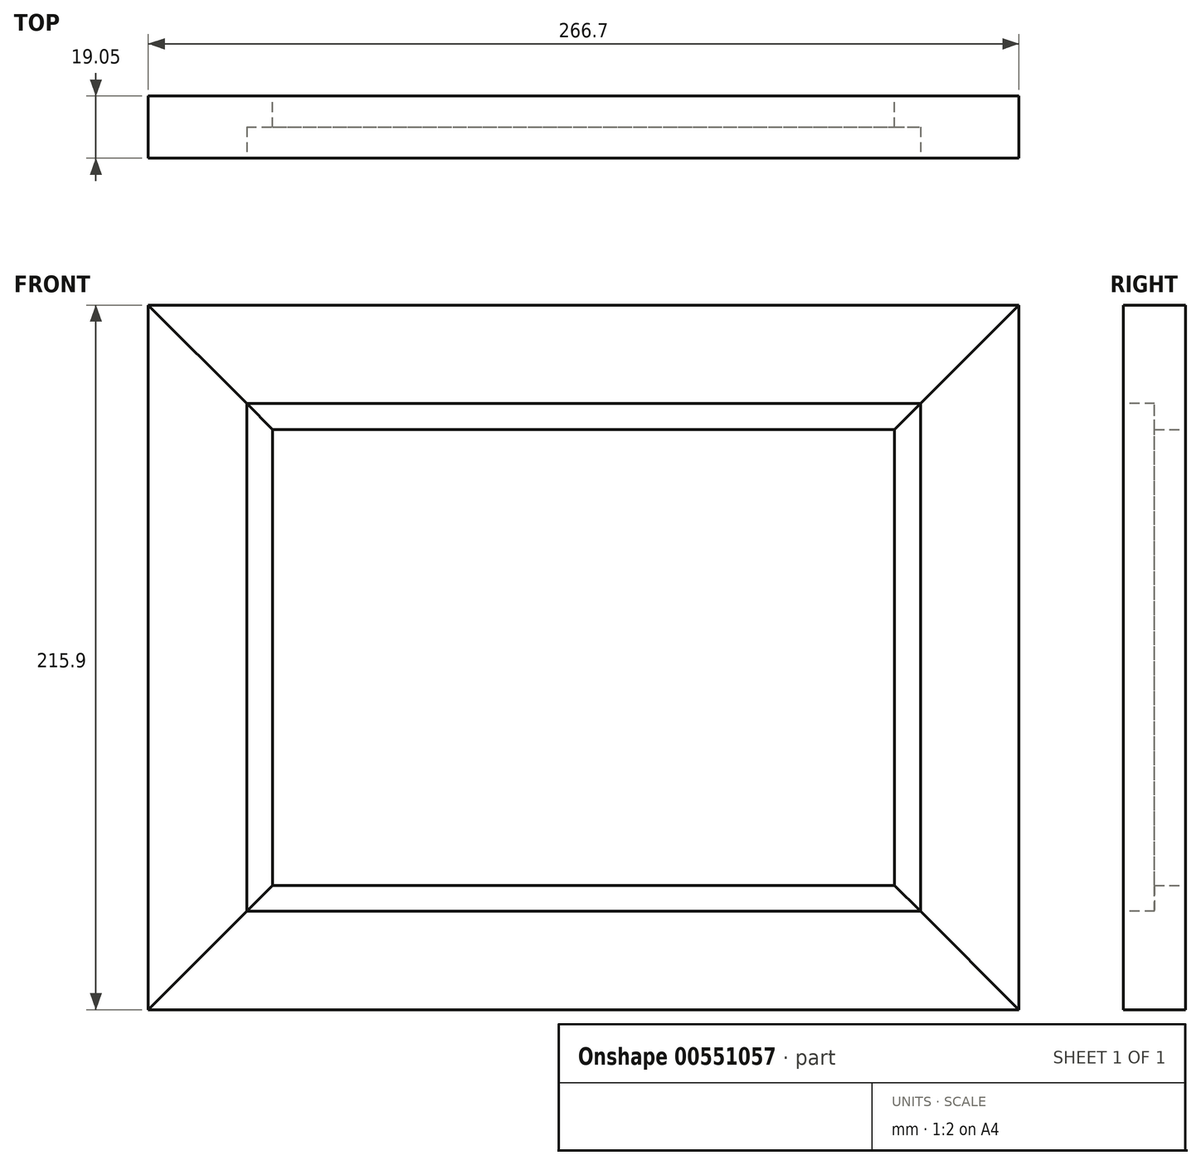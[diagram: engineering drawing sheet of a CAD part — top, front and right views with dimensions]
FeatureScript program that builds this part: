
annotation { "Feature Type Name" : "Feature", "Feature Type Description" : "" }
export const myFeature = defineFeature(function(context is Context, id is Id, definition is map)
    precondition{}
    {
        {
            var Q0;
            Q0=qCreatedBy(makeId("Front.planeOp"),FACE);
            var sketch = newSketch(context, id + "F0", { "sketchPlane" : qUnion([Q0])});
            skLineSegment(sketch, "E0", {"start": v(0, 0) * mm, "end": v(0, 139.7) * mm});
            skLineSegment(sketch, "E1", {"start": v(0, 139.7) * mm, "end": v(-38.1, 177.8) * mm});
            skLineSegment(sketch, "E2", {"start": v(-38.1, 177.8) * mm, "end": v(-38.1, -38.1) * mm});
            skLineSegment(sketch, "E3", {"start": v(-38.1, -38.1) * mm, "end": v(0, 0) * mm});
            skLineSegment(sketch, "E4", {"start": v(0, 139.7) * mm, "end": v(190.5, 139.7) * mm});
            skLineSegment(sketch, "E5", {"start": v(190.5, 139.7) * mm, "end": v(228.6, 177.8) * mm});
            skLineSegment(sketch, "E6", {"start": v(228.6, 177.8) * mm, "end": v(-38.1, 177.8) * mm});
            skLineSegment(sketch, "E7", {"start": v(0, 0) * mm, "end": v(190.5, 0) * mm});
            skLineSegment(sketch, "E8", {"start": v(190.5, 0) * mm, "end": v(190.5, 139.7) * mm});
            skLineSegment(sketch, "E9", {"start": v(190.5, 0) * mm, "end": v(228.6, -38.1) * mm});
            skLineSegment(sketch, "E10", {"start": v(228.6, -38.1) * mm, "end": v(228.6, 177.8) * mm});
            skLineSegment(sketch, "E11", {"start": v(-38.1, -38.1) * mm, "end": v(228.6, -38.1) * mm});
            skSolve(sketch);
        }
        {
            var Q0;
            Q0=makeQuery(id+"F0.imprint","IMPRINT",FACE,{"disambiguationData":[TD([[makeQuery(id+"F0.imprint","IMPRINT",EDGE,{"derivedFrom":sQuery(id+"F0.wireOp",EDGE,"E0")}),1.0]])]});
            extrude(context, id + "F1", {"entities" : qUnion([Q0]), "depth" : 19.05 * mm, "offsetDistance" : 25.4 * mm});
        }
        {
            var Q0;
            Q0=makeQuery(id+"F0.imprint","IMPRINT",FACE,{"disambiguationData":[TD([[makeQuery(id+"F0.imprint","IMPRINT",EDGE,{"derivedFrom":sQuery(id+"F0.wireOp",EDGE,"E1")}),-1.0]])]});
            extrude(context, id + "F2", {"entities" : qUnion([Q0]), "depth" : 19.05 * mm, "offsetDistance" : 25.4 * mm});
        }
        {
            var Q0;
            Q0=makeQuery(id+"F0.imprint","IMPRINT",FACE,{"disambiguationData":[TD([[makeQuery(id+"F0.imprint","IMPRINT",EDGE,{"derivedFrom":sQuery(id+"F0.wireOp",EDGE,"E5")}),-1.0]])]});
            extrude(context, id + "F3", {"entities" : qUnion([Q0]), "depth" : 19.05 * mm, "offsetDistance" : 25.4 * mm});
        }
        {
            var Q0;
            Q0=makeQuery(id+"F0.imprint","IMPRINT",FACE,{"disambiguationData":[TD([[makeQuery(id+"F0.imprint","IMPRINT",EDGE,{"derivedFrom":sQuery(id+"F0.wireOp",EDGE,"E3")}),-1.0]])]});
            extrude(context, id + "F4", {"entities" : qUnion([Q0]), "depth" : 19.05 * mm, "offsetDistance" : 25.4 * mm});
        }
        {
            var Q0;
            Q0=makeQuery(id+"F2.opExtrude","CAP_FACE",FACE,{"disambiguationData":[OSD([sQuery(id+"F0.wireOp",EDGE,"E1"),sQuery(id+"F0.wireOp",EDGE,"E4"),sQuery(id+"F0.wireOp",EDGE,"E5"),sQuery(id+"F0.wireOp",EDGE,"E6")])],"isStart":false});
            var sketch = newSketch(context, id + "F5", { "sketchPlane" : qUnion([Q0])});
            skLineSegment(sketch, "E12.0", {"start": v(0, 139.7) * mm, "end": v(-38.1, 177.8) * mm});
            skLineSegment(sketch, "E13.0", {"start": v(-38.1, -38.1) * mm, "end": v(0, 0) * mm});
            skLineSegment(sketch, "E14.0", {"start": v(190.5, 0) * mm, "end": v(228.6, -38.1) * mm});
            skLineSegment(sketch, "E15.0", {"start": v(190.5, 139.7) * mm, "end": v(228.6, 177.8) * mm});
            skLineSegment(sketch, "E16.0", {"start": v(190.5, 0) * mm, "end": v(190.5, 139.7) * mm});
            skLineSegment(sketch, "E17.0", {"start": v(0, 139.7) * mm, "end": v(190.5, 139.7) * mm});
            skLineSegment(sketch, "E18.0", {"start": v(0, 0) * mm, "end": v(0, 139.7) * mm});
            skLineSegment(sketch, "E19.0", {"start": v(0, 0) * mm, "end": v(190.5, 0) * mm});
            skLineSegment(sketch, "E20.bottom", {"start": v(-7.94, -7.94) * mm, "end": v(198.44, -7.94) * mm});
            skLineSegment(sketch, "E20.top", {"start": v(-7.94, 147.64) * mm, "end": v(198.44, 147.64) * mm});
            skLineSegment(sketch, "E20.left", {"start": v(-7.94, -7.94) * mm, "end": v(-7.94, 147.64) * mm});
            skLineSegment(sketch, "E20.right", {"start": v(198.44, -7.94) * mm, "end": v(198.44, 147.64) * mm});
            skSolve(sketch);
        }
        {
            var Q0;
            {var subQ0=sQuery(id+"F5.wireOp",EDGE,"E17.0");Q0=makeQuery(id+"F5.imprint","IMPRINT",FACE,{"disambiguationData":[TD([[makeQuery(id+"F5.imprint","IMPRINT",EDGE,{"derivedFrom":subQ0}),1.0]])]});}
            var Q1;
            {var subQ0=sQuery(id+"F5.wireOp",EDGE,"E18.0");Q1=makeQuery(id+"F5.imprint","IMPRINT",FACE,{"disambiguationData":[TD([[makeQuery(id+"F5.imprint","IMPRINT",EDGE,{"derivedFrom":subQ0}),1.0]])]});}
            var Q2;
            {var subQ0=sQuery(id+"F5.wireOp",EDGE,"E19.0");Q2=makeQuery(id+"F5.imprint","IMPRINT",FACE,{"disambiguationData":[TD([[makeQuery(id+"F5.imprint","IMPRINT",EDGE,{"derivedFrom":subQ0}),-1.0]])]});}
            var Q3;
            {var subQ0=sQuery(id+"F5.wireOp",EDGE,"E16.0");Q3=makeQuery(id+"F5.imprint","IMPRINT",FACE,{"disambiguationData":[TD([[makeQuery(id+"F5.imprint","IMPRINT",EDGE,{"derivedFrom":subQ0}),-1.0]])]});}
            extrude(context, id + "F6", {"entities" : qUnion([Q0, Q1, Q2, Q3]), "operationType" : NewBodyOperationType.REMOVE, "oppositeDirection" : true, "depth" : 9.52 * mm, "offsetDistance" : 25.4 * mm});
        }
    });
